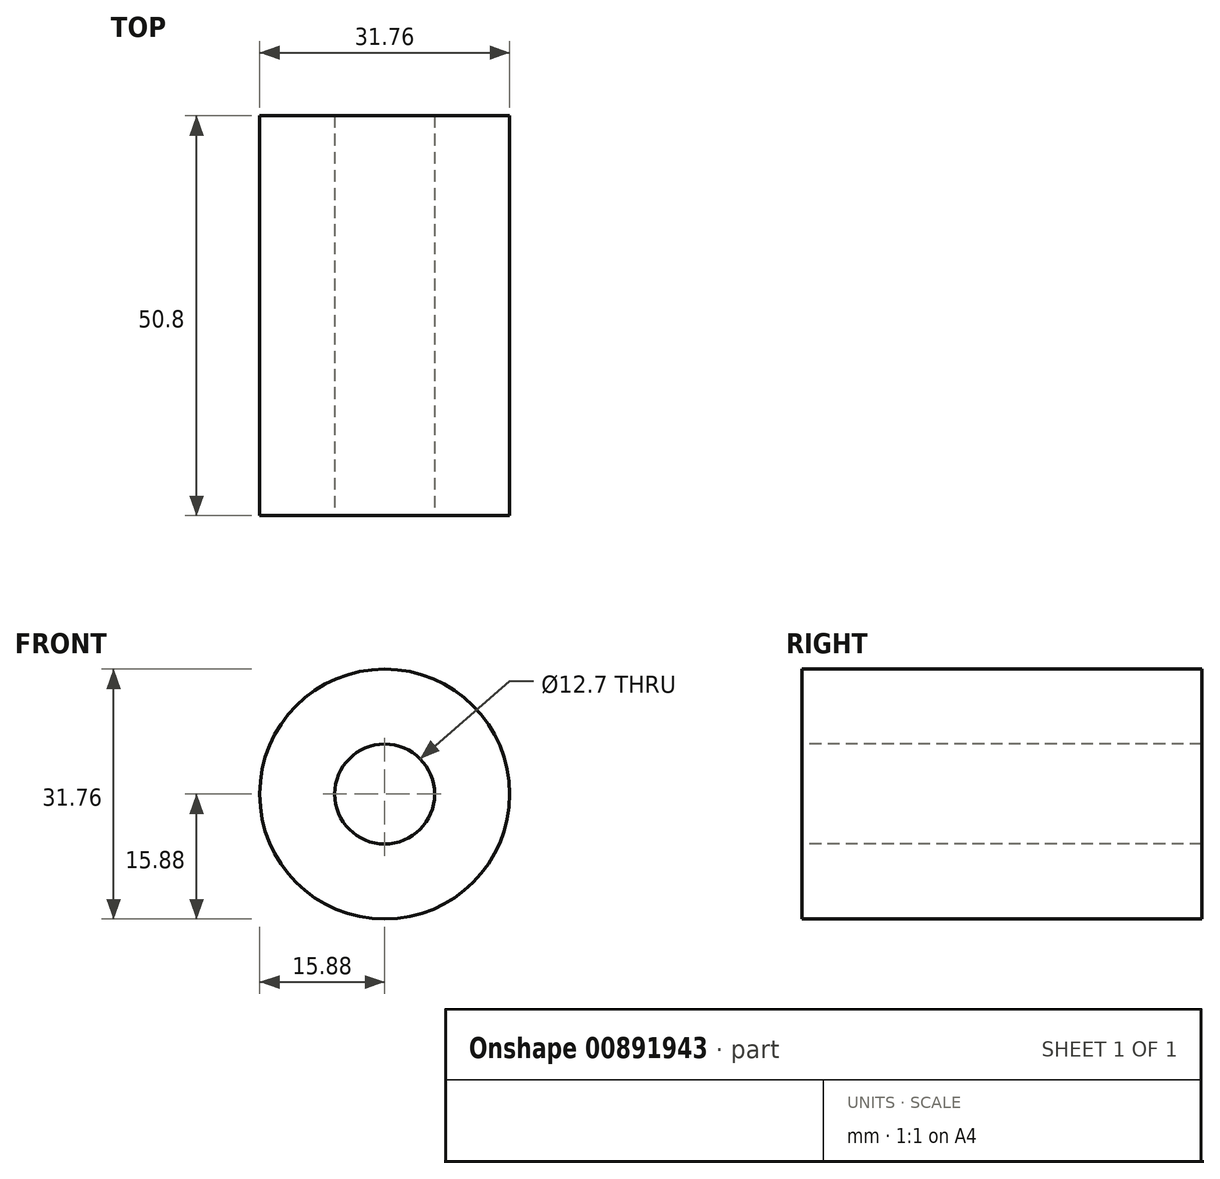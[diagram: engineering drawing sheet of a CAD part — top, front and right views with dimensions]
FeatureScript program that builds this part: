
annotation { "Feature Type Name" : "Feature", "Feature Type Description" : "" }
export const myFeature = defineFeature(function(context is Context, id is Id, definition is map)
    precondition{}
    {
        {
            var Q0;
            Q0=qCreatedBy(makeId("Front.planeOp"),FACE);
            var sketch = newSketch(context, id + "F0", { "sketchPlane" : qUnion([Q0])});
            skCircle(sketch, "E0", {"center": v(0, 0) * mm, "radius": 15.88 * mm});
            skCircle(sketch, "E1", {"center": v(0, 0) * mm, "radius": 6.35 * mm});
            skSolve(sketch);
        }
        {
            var Q0;
            Q0=makeQuery(id+"F0.imprint","IMPRINT",FACE,{"disambiguationData":[TD([[makeQuery(id+"F0.imprint","IMPRINT",EDGE,{"derivedFrom":sQuery(id+"F0.wireOp",EDGE,"E0")}),1.0]])]});
            extrude(context, id + "F1", {"entities" : qUnion([Q0]), "endBound" : BoundingType.SYMMETRIC, "oppositeDirection" : true, "depth" : 50.8 * mm, "offsetDistance" : 25.4 * mm});
        }
    });
